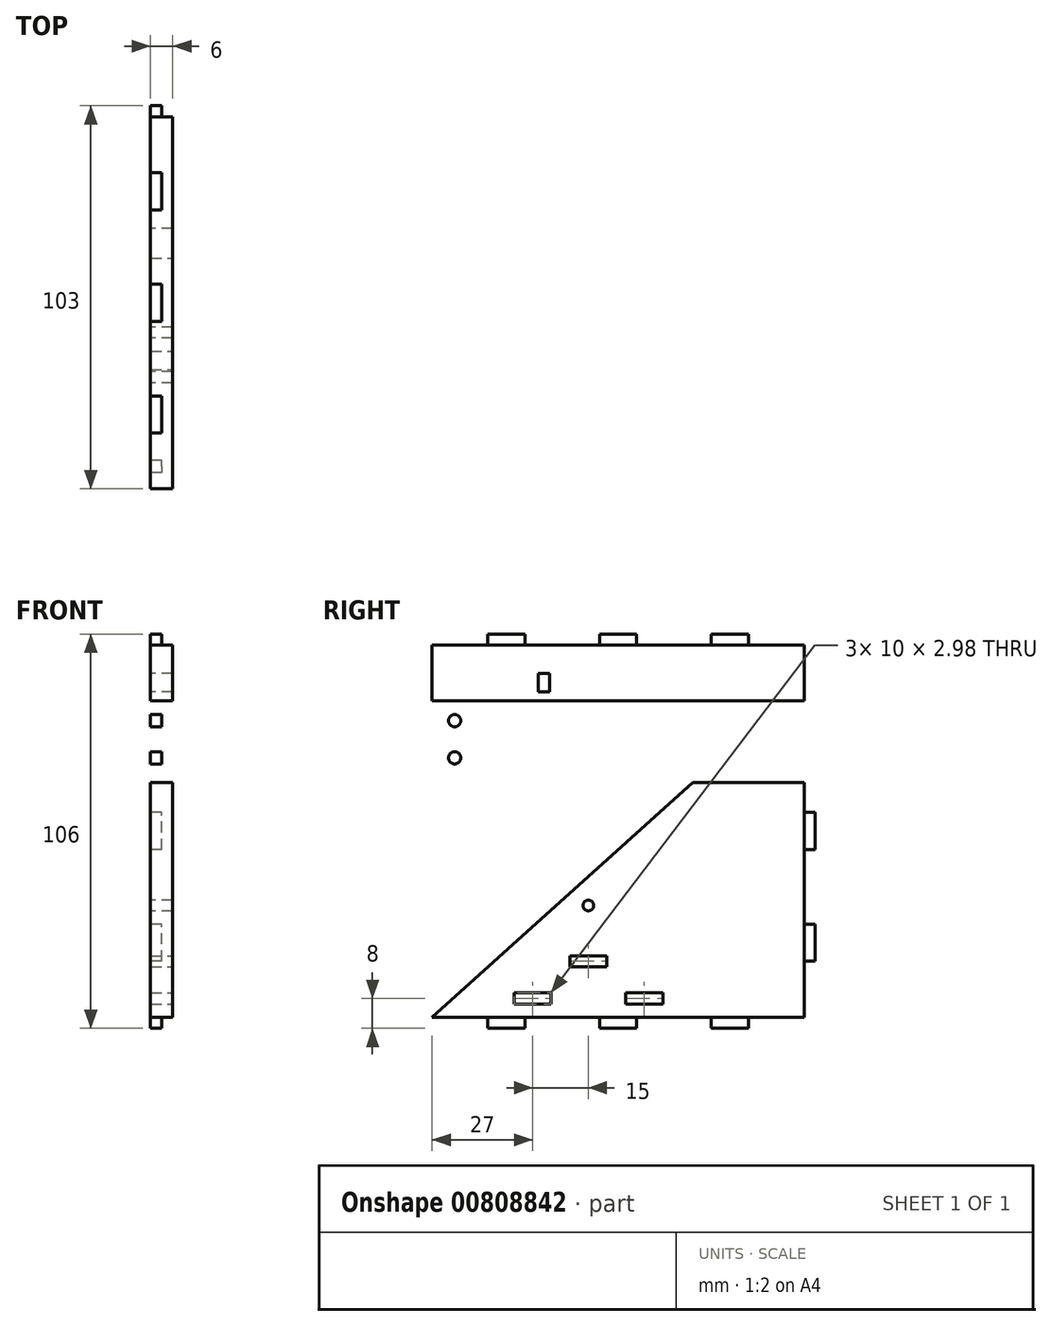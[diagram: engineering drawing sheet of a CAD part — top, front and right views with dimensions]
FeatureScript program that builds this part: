
annotation { "Feature Type Name" : "Feature", "Feature Type Description" : "" }
export const myFeature = defineFeature(function(context is Context, id is Id, definition is map)
    precondition{}
    {
        {
            var Q0;
            Q0=qCreatedBy(makeId("Right.planeOp"),FACE);
            var sketch = newSketch(context, id + "F0", { "sketchPlane" : qUnion([Q0])});
            skLineSegment(sketch, "E0.bottom", {"start": v(-50, 50) * mm, "end": v(50, 50) * mm});
            skLineSegment(sketch, "E0.top", {"start": v(-50, -50) * mm, "end": v(50, -50) * mm});
            skLineSegment(sketch, "E0.left", {"start": v(-50, 50) * mm, "end": v(-50, -50) * mm});
            skLineSegment(sketch, "E0.right", {"start": v(50, 50) * mm, "end": v(50, -50) * mm});
            skPoint(sketch, "E0.middle", {"position": v(0, 0) * mm});
            skLineSegment(sketch, "E1.bottom", {"start": v(-5, 47) * mm, "end": v(5, 47) * mm});
            skLineSegment(sketch, "E1.top", {"start": v(-5, 53) * mm, "end": v(5, 53) * mm});
            skLineSegment(sketch, "E1.left", {"start": v(-5, 47) * mm, "end": v(-5, 53) * mm});
            skLineSegment(sketch, "E1.right", {"start": v(5, 47) * mm, "end": v(5, 53) * mm});
            skPoint(sketch, "E1.middle", {"position": v(0, 50) * mm});
            skLineSegment(sketch, "E2.bottom", {"start": v(35, 53) * mm, "end": v(25, 53) * mm});
            skLineSegment(sketch, "E2.top", {"start": v(35, 47) * mm, "end": v(25, 47) * mm});
            skLineSegment(sketch, "E2.left", {"start": v(35, 53) * mm, "end": v(35, 47) * mm});
            skLineSegment(sketch, "E2.right", {"start": v(25, 53) * mm, "end": v(25, 47) * mm});
            skPoint(sketch, "E2.middle", {"position": v(30, 50) * mm});
            skLineSegment(sketch, "E3.bottom", {"start": v(-35, 53) * mm, "end": v(-25, 53) * mm});
            skLineSegment(sketch, "E3.top", {"start": v(-35, 47) * mm, "end": v(-25, 47) * mm});
            skLineSegment(sketch, "E3.left", {"start": v(-35, 53) * mm, "end": v(-35, 47) * mm});
            skLineSegment(sketch, "E3.right", {"start": v(-25, 53) * mm, "end": v(-25, 47) * mm});
            skPoint(sketch, "E3.middle", {"position": v(-30, 50) * mm});
            skLineSegment(sketch, "E4.1.0", {"start": v(-53, 25) * mm, "end": v(-47, 25) * mm});
            skLineSegment(sketch, "E4.1.1", {"start": v(-53, 35) * mm, "end": v(-53, 25) * mm});
            skLineSegment(sketch, "E4.1.2", {"start": v(-53, 35) * mm, "end": v(-47, 35) * mm});
            skLineSegment(sketch, "E4.1.3", {"start": v(-47, 35) * mm, "end": v(-47, 25) * mm});
            skLineSegment(sketch, "E4.1.4", {"start": v(-47, -5) * mm, "end": v(-47, 5) * mm});
            skLineSegment(sketch, "E4.1.5", {"start": v(-47, 5) * mm, "end": v(-53, 5) * mm});
            skLineSegment(sketch, "E4.1.6", {"start": v(-53, -5) * mm, "end": v(-53, 5) * mm});
            skLineSegment(sketch, "E4.1.7", {"start": v(-47, -5) * mm, "end": v(-53, -5) * mm});
            skLineSegment(sketch, "E4.1.8", {"start": v(-53, -35) * mm, "end": v(-53, -25) * mm});
            skLineSegment(sketch, "E4.1.9", {"start": v(-47, -35) * mm, "end": v(-47, -25) * mm});
            skLineSegment(sketch, "E4.1.10", {"start": v(-53, -25) * mm, "end": v(-47, -25) * mm});
            skLineSegment(sketch, "E4.1.11", {"start": v(-53, -35) * mm, "end": v(-47, -35) * mm});
            skLineSegment(sketch, "E4.2.0", {"start": v(-25, -53) * mm, "end": v(-25, -47) * mm});
            skLineSegment(sketch, "E4.2.1", {"start": v(-35, -53) * mm, "end": v(-25, -53) * mm});
            skLineSegment(sketch, "E4.2.2", {"start": v(-35, -53) * mm, "end": v(-35, -47) * mm});
            skLineSegment(sketch, "E4.2.3", {"start": v(-35, -47) * mm, "end": v(-25, -47) * mm});
            skLineSegment(sketch, "E4.2.4", {"start": v(5, -47) * mm, "end": v(-5, -47) * mm});
            skLineSegment(sketch, "E4.2.5", {"start": v(-5, -47) * mm, "end": v(-5, -53) * mm});
            skLineSegment(sketch, "E4.2.6", {"start": v(5, -53) * mm, "end": v(-5, -53) * mm});
            skLineSegment(sketch, "E4.2.7", {"start": v(5, -47) * mm, "end": v(5, -53) * mm});
            skLineSegment(sketch, "E4.2.8", {"start": v(35, -53) * mm, "end": v(25, -53) * mm});
            skLineSegment(sketch, "E4.2.9", {"start": v(35, -47) * mm, "end": v(25, -47) * mm});
            skLineSegment(sketch, "E4.2.10", {"start": v(25, -53) * mm, "end": v(25, -47) * mm});
            skLineSegment(sketch, "E4.2.11", {"start": v(35, -53) * mm, "end": v(35, -47) * mm});
            skLineSegment(sketch, "E4.3.0", {"start": v(53, -25) * mm, "end": v(47, -25) * mm});
            skLineSegment(sketch, "E4.3.1", {"start": v(53, -35) * mm, "end": v(53, -25) * mm});
            skLineSegment(sketch, "E4.3.2", {"start": v(53, -35) * mm, "end": v(47, -35) * mm});
            skLineSegment(sketch, "E4.3.3", {"start": v(47, -35) * mm, "end": v(47, -25) * mm});
            skLineSegment(sketch, "E4.3.4", {"start": v(47, 5) * mm, "end": v(47, -5) * mm});
            skLineSegment(sketch, "E4.3.5", {"start": v(47, -5) * mm, "end": v(53, -5) * mm});
            skLineSegment(sketch, "E4.3.6", {"start": v(53, 5) * mm, "end": v(53, -5) * mm});
            skLineSegment(sketch, "E4.3.7", {"start": v(47, 5) * mm, "end": v(53, 5) * mm});
            skLineSegment(sketch, "E4.3.8", {"start": v(53, 35) * mm, "end": v(53, 25) * mm});
            skLineSegment(sketch, "E4.3.9", {"start": v(47, 35) * mm, "end": v(47, 25) * mm});
            skLineSegment(sketch, "E4.3.10", {"start": v(53, 25) * mm, "end": v(47, 25) * mm});
            skLineSegment(sketch, "E4.3.11", {"start": v(53, 35) * mm, "end": v(47, 35) * mm});
            skCircle(sketch, "E5", {"center": v(-8, -20) * mm, "radius": 1.45 * mm});
            skSolve(sketch);
        }
        {
            var Q0;
            Q0=qSketchRegion(id+"F0",true);
            extrude(context, id + "F1", {"entities" : qUnion([Q0]), "depth" : 3 * mm, "offsetDistance" : 25 * mm});
        }
        {
            var Q0;
            Q0=makeQuery(id+"F1.opExtrude","CAP_FACE",FACE,{"disambiguationData":[OSD([sQuery(id+"F0.wireOp",EDGE,"E0.bottom"),sQuery(id+"F0.wireOp",EDGE,"E0.top"),sQuery(id+"F0.wireOp",EDGE,"E0.left"),sQuery(id+"F0.wireOp",EDGE,"E0.right"),sQuery(id+"F0.wireOp",EDGE,"E1.top"),sQuery(id+"F0.wireOp",EDGE,"E1.left"),sQuery(id+"F0.wireOp",EDGE,"E1.right"),sQuery(id+"F0.wireOp",EDGE,"E2.bottom"),sQuery(id+"F0.wireOp",EDGE,"E2.left"),sQuery(id+"F0.wireOp",EDGE,"E2.right"),sQuery(id+"F0.wireOp",EDGE,"E3.bottom"),sQuery(id+"F0.wireOp",EDGE,"E3.left"),sQuery(id+"F0.wireOp",EDGE,"E3.right"),sQuery(id+"F0.wireOp",EDGE,"E4.1.0"),sQuery(id+"F0.wireOp",EDGE,"E4.1.1"),sQuery(id+"F0.wireOp",EDGE,"E4.1.2"),sQuery(id+"F0.wireOp",EDGE,"E4.1.5"),sQuery(id+"F0.wireOp",EDGE,"E4.1.6"),sQuery(id+"F0.wireOp",EDGE,"E4.1.7"),sQuery(id+"F0.wireOp",EDGE,"E4.1.8"),sQuery(id+"F0.wireOp",EDGE,"E4.1.10"),sQuery(id+"F0.wireOp",EDGE,"E4.1.11"),sQuery(id+"F0.wireOp",EDGE,"E4.2.0"),sQuery(id+"F0.wireOp",EDGE,"E4.2.1"),sQuery(id+"F0.wireOp",EDGE,"E4.2.2"),sQuery(id+"F0.wireOp",EDGE,"E4.2.5"),sQuery(id+"F0.wireOp",EDGE,"E4.2.6"),sQuery(id+"F0.wireOp",EDGE,"E4.2.7"),sQuery(id+"F0.wireOp",EDGE,"E4.2.8"),sQuery(id+"F0.wireOp",EDGE,"E4.2.10"),sQuery(id+"F0.wireOp",EDGE,"E4.2.11"),sQuery(id+"F0.wireOp",EDGE,"E4.3.0"),sQuery(id+"F0.wireOp",EDGE,"E4.3.1"),sQuery(id+"F0.wireOp",EDGE,"E4.3.2"),sQuery(id+"F0.wireOp",EDGE,"E4.3.5"),sQuery(id+"F0.wireOp",EDGE,"E4.3.6"),sQuery(id+"F0.wireOp",EDGE,"E4.3.7"),sQuery(id+"F0.wireOp",EDGE,"E4.3.8"),sQuery(id+"F0.wireOp",EDGE,"E4.3.10"),sQuery(id+"F0.wireOp",EDGE,"E4.3.11")])],"isStart":true});
            var sketch = newSketch(context, id + "F2", { "sketchPlane" : qUnion([Q0])});
            skLineSegment(sketch, "E6", {"start": v(-50, -50) * mm, "end": v(50, -50) * mm});
            skLineSegment(sketch, "E7", {"start": v(50, -50) * mm, "end": v(-20, 13) * mm});
            skLineSegment(sketch, "E8", {"start": v(-20, 13) * mm, "end": v(-50, 13) * mm});
            skLineSegment(sketch, "E9", {"start": v(-50, 13) * mm, "end": v(-50, -50) * mm});
            skLineSegment(sketch, "E10", {"start": v(0, 0) * mm, "end": v(0, 15) * mm});
            skLineSegment(sketch, "E11", {"start": v(-50, 35) * mm, "end": v(50, 35) * mm});
            skLineSegment(sketch, "E12", {"start": v(50, 50) * mm, "end": v(-50, 50) * mm});
            skLineSegment(sketch, "E13", {"start": v(-50, 50) * mm, "end": v(-50, 35) * mm});
            skLineSegment(sketch, "E14", {"start": v(50, 35) * mm, "end": v(50, 50) * mm});
            skLineSegment(sketch, "E15.top", {"start": v(0, 34.4) * mm, "end": v(39.9, 34.4) * mm});
            skLineSegment(sketch, "E15.left", {"start": v(0, 15) * mm, "end": v(0, 34.4) * mm});
            skLineSegment(sketch, "E15.right", {"start": v(39.9, 15) * mm, "end": v(39.9, 34.4) * mm});
            skLineSegment(sketch, "E16", {"start": v(0, 24.7) * mm, "end": v(39.9, 24.7) * mm, "construction": true});
            skLineSegment(sketch, "E17", {"start": v(19.95, 34.4) * mm, "end": v(19.95, 15) * mm, "construction": true});
            skLineSegment(sketch, "E18.MirrorCS", {"start": v(39.9, 15) * mm, "end": v(0, 15) * mm});
            skCircle(sketch, "E19", {"center": v(-4.05, 29.7) * mm, "radius": 1.65 * mm});
            skCircle(sketch, "E20.0.1.0", {"center": v(-4.05, 19.7) * mm, "radius": 1.65 * mm});
            skLineSegment(sketch, "E20.direction1", {"start": v(-4.05, 29.7) * mm, "end": v(20.95, 29.7) * mm, "construction": true});
            skLineSegment(sketch, "E20.direction2", {"start": v(-4.05, 29.7) * mm, "end": v(-4.05, 19.7) * mm, "construction": true});
            skCircle(sketch, "E21.MirrorC", {"center": v(43.95, 29.7) * mm, "radius": 1.65 * mm});
            skCircle(sketch, "E22.MirrorC", {"center": v(43.95, 19.7) * mm, "radius": 1.65 * mm});
            skLineSegment(sketch, "E23.MirrorCS", {"start": v(43.95, 29.7) * mm, "end": v(43.95, 19.7) * mm, "construction": true});
            skLineSegment(sketch, "E24.MirrorCS", {"start": v(43.95, 29.7) * mm, "end": v(18.95, 29.7) * mm, "construction": true});
            skLineSegment(sketch, "E25", {"start": v(9.98, 15) * mm, "end": v(9.98, 12) * mm, "construction": true});
            skLineSegment(sketch, "E26.bottom", {"start": v(9.98, 12) * mm, "end": v(12.96, 12) * mm});
            skLineSegment(sketch, "E26.top", {"start": v(9.98, 7) * mm, "end": v(12.96, 7) * mm});
            skLineSegment(sketch, "E26.left", {"start": v(9.98, 12) * mm, "end": v(9.98, 7) * mm});
            skLineSegment(sketch, "E26.right", {"start": v(12.96, 12) * mm, "end": v(12.96, 7) * mm});
            skLineSegment(sketch, "E27.MirrorCS", {"start": v(29.92, 15) * mm, "end": v(29.92, 12) * mm, "construction": true});
            skLineSegment(sketch, "E28.MirrorCS", {"start": v(29.92, 7) * mm, "end": v(26.94, 7) * mm});
            skLineSegment(sketch, "E29.MirrorCS", {"start": v(29.92, 12) * mm, "end": v(29.92, 7) * mm});
            skLineSegment(sketch, "E30.MirrorCS", {"start": v(26.94, 12) * mm, "end": v(26.94, 7) * mm});
            skLineSegment(sketch, "E31.MirrorCS", {"start": v(29.92, 12) * mm, "end": v(26.94, 12) * mm});
            skLineSegment(sketch, "E32", {"start": v(19.95, 34.4) * mm, "end": v(19.95, 37.4) * mm, "construction": true});
            skLineSegment(sketch, "E33.bottom", {"start": v(18.46, 37.4) * mm, "end": v(21.44, 37.4) * mm});
            skLineSegment(sketch, "E33.top", {"start": v(18.46, 42.4) * mm, "end": v(21.44, 42.4) * mm});
            skLineSegment(sketch, "E33.left", {"start": v(18.46, 37.4) * mm, "end": v(18.46, 42.4) * mm});
            skLineSegment(sketch, "E33.right", {"start": v(21.44, 37.4) * mm, "end": v(21.44, 42.4) * mm});
            skSolve(sketch);
        }
        {
            var Q0;
            Q0=makeQuery(id+"F2.imprint","IMPRINT",FACE,{"disambiguationData":[TD([[makeQuery(id+"F2.imprint","IMPRINT",EDGE,{"derivedFrom":sQuery(id+"F2.wireOp",EDGE,"E19")}),1.0]])]});
            var Q1;
            Q1=makeQuery(id+"F2.imprint","IMPRINT",FACE,{"disambiguationData":[TD([[makeQuery(id+"F2.imprint","IMPRINT",EDGE,{"derivedFrom":sQuery(id+"F2.wireOp",EDGE,"E20.0.1.0")}),1.0]])]});
            var Q2;
            Q2=makeQuery(id+"F2.imprint","IMPRINT",FACE,{"disambiguationData":[TD([[makeQuery(id+"F2.imprint","IMPRINT",EDGE,{"derivedFrom":sQuery(id+"F2.wireOp",EDGE,"E21.MirrorC")}),-1.0]])]});
            var Q3;
            Q3=makeQuery(id+"F2.imprint","IMPRINT",FACE,{"disambiguationData":[TD([[makeQuery(id+"F2.imprint","IMPRINT",EDGE,{"derivedFrom":sQuery(id+"F2.wireOp",EDGE,"E22.MirrorC")}),-1.0]])]});
            var Q4;
            Q4=makeQuery(id+"F2.imprint","IMPRINT",FACE,{"disambiguationData":[TD([[makeQuery(id+"F2.imprint","IMPRINT",EDGE,{"derivedFrom":sQuery(id+"F2.wireOp",EDGE,"E26.bottom")}),-1.0]])]});
            var Q5;
            Q5=makeQuery(id+"F2.imprint","IMPRINT",FACE,{"disambiguationData":[TD([[makeQuery(id+"F2.imprint","IMPRINT",EDGE,{"derivedFrom":sQuery(id+"F2.wireOp",EDGE,"E28.MirrorCS")}),-1.0]])]});
            var Q6;
            Q6=makeQuery(id+"F2.imprint","IMPRINT",FACE,{"disambiguationData":[TD([[makeQuery(id+"F2.imprint","IMPRINT",EDGE,{"derivedFrom":sQuery(id+"F2.wireOp",EDGE,"E15.top")}),-1.0]])]});
            var Q7;
            Q7=makeQuery(id+"F2.imprint","IMPRINT",FACE,{"disambiguationData":[TD([[makeQuery(id+"F2.imprint","IMPRINT",EDGE,{"derivedFrom":sQuery(id+"F2.wireOp",EDGE,"E33.bottom")}),1.0]])]});
            extrude(context, id + "F3", {"entities" : qUnion([Q0, Q1, Q2, Q3, Q4, Q5, Q6, Q7]), "operationType" : NewBodyOperationType.REMOVE, "oppositeDirection" : true, "depth" : 25 * mm, "offsetDistance" : 25 * mm});
        }
        {
            var Q0;
            Q0=makeQuery(id+"F2.imprint","IMPRINT",FACE,{"disambiguationData":[TD([[makeQuery(id+"F2.imprint","IMPRINT",EDGE,{"derivedFrom":sQuery(id+"F2.wireOp",EDGE,"E11")}),1.0]])]});
            var Q1;
            {var subQ5=sQuery(id+"F2.wireOp",EDGE,"E7");Q1=makeQuery(id+"F2.imprint","IMPRINT",FACE,{"disambiguationData":[TD([[makeQuery(id+"F2.imprint","IMPRINT",EDGE,{"derivedFrom":subQ5}),1.0]])]});}
            extrude(context, id + "F4", {"entities" : qUnion([Q0, Q1]), "operationType" : NewBodyOperationType.ADD, "oppositeDirection" : true, "depth" : 6 * mm, "offsetDistance" : 25 * mm});
        }
        {
            var Q0;
            Q0=qCreatedBy(makeId("Right.planeOp"),FACE);
            var sketch = newSketch(context, id + "F5", { "sketchPlane" : qUnion([Q0])});
            skLineSegment(sketch, "E34.bottom", {"start": v(-50, -50) * mm, "end": v(50, -50) * mm});
            skLineSegment(sketch, "E34.top", {"start": v(-50, 50) * mm, "end": v(50, 50) * mm});
            skLineSegment(sketch, "E34.right", {"start": v(50, -50) * mm, "end": v(50, 50) * mm});
            skPoint(sketch, "E34.middle", {"position": v(0, 0) * mm});
            skLineSegment(sketch, "E35.bottom", {"start": v(-28, -43.5) * mm, "end": v(-18, -43.5) * mm});
            skLineSegment(sketch, "E35.top", {"start": v(-28, -46.5) * mm, "end": v(-18, -46.5) * mm});
            skLineSegment(sketch, "E35.left", {"start": v(-28, -43.5) * mm, "end": v(-28, -46.5) * mm});
            skLineSegment(sketch, "E35.right", {"start": v(-18, -43.5) * mm, "end": v(-18, -46.5) * mm});
            skPoint(sketch, "E35.middle", {"position": v(-23, -45) * mm});
            skLineSegment(sketch, "E36.bottom", {"start": v(-3, -36.5) * mm, "end": v(-13, -36.5) * mm});
            skLineSegment(sketch, "E36.top", {"start": v(-3, -33.5) * mm, "end": v(-13, -33.5) * mm});
            skLineSegment(sketch, "E36.left", {"start": v(-3, -36.5) * mm, "end": v(-3, -33.5) * mm});
            skLineSegment(sketch, "E36.right", {"start": v(-13, -36.5) * mm, "end": v(-13, -33.5) * mm});
            skPoint(sketch, "E36.middle", {"position": v(-8, -35) * mm});
            skLineSegment(sketch, "E37.bottom", {"start": v(12, -46.5) * mm, "end": v(2, -46.5) * mm});
            skLineSegment(sketch, "E37.top", {"start": v(12, -43.5) * mm, "end": v(2, -43.5) * mm});
            skLineSegment(sketch, "E37.left", {"start": v(12, -46.5) * mm, "end": v(12, -43.5) * mm});
            skLineSegment(sketch, "E37.right", {"start": v(2, -46.5) * mm, "end": v(2, -43.5) * mm});
            skPoint(sketch, "E37.middle", {"position": v(7, -45) * mm});
            skSolve(sketch);
        }
        {
            var Q0;
            Q0=qSketchRegion(id+"F5",true);
            extrude(context, id + "F6", {"entities" : qUnion([Q0]), "operationType" : NewBodyOperationType.REMOVE, "oppositeDirection" : true, "depth" : 25 * mm, "offsetDistance" : 25 * mm, "symmetric" : true});
        }
    });
